# Revit family: MV8-252(280_335_400_450)WV2GN1(PRO)
name_source: partatom
category: Mechanical Equipment
revit_build: Autodesk Revit 2013 (Build: 20120221_2030(x64)
units: mm (PartAtom-declared; Revit-internal decimal feet)

## types (5) — shared parameters
Casing color = White
Compressor = 1
Condensation = Air
Depth = 825 mm  [stored 2.70669 ft]
Description = High efficiency air cooled
Gas = R410A
Height = 1760 mm  [stored 5.77428 ft]
Installation = Outdoor installation
Machine material = Galvanized Steel
Power supply = 380-415V, 3N , 50Hz
Series = VRF
Width = 940 mm  [stored 3.08399 ft]
clearance access behind = 1000 mm  [stored 3.28084 ft]
clearance access front = 1000 mm  [stored 3.28084 ft]
clearance access left = 1000 mm  [stored 3.28084 ft]
clearance access right = 1000 mm  [stored 3.28084 ft]

## per-type parameters (varying)
| type | Air Flow | Cooling Capacity | Cooling Power Input | Gas pipe | Gas pipe Radius | Heating Capacity | Heating Power Input | Liquid pipe | Liquid pipe Radius | Maximum Fuse Amps | Minimum Circuit Amps | Net Weight |
| 12HP | 13500.000 m³/h | 33.500 kW | 13.500 kW | 25.4 mm  [stored 0.0833333 ft] | 12.7 mm  [stored 0.0416667 ft] | 33.500 kW | 10.800 kW | 12.7 mm  [stored 0.0416667 ft] | 6.35 mm  [stored 0.0208333 ft] | 32 A | 23 A | 195.00 kg |
| 10HP | 12600.000 m³/h | 28.000 kW | 9.900 kW | 25.4 mm  [stored 0.0833333 ft] | 12.7 mm  [stored 0.0416667 ft] | 28.000 kW | 7.500 kW | 12.7 mm  [stored 0.0416667 ft] | 6.35 mm  [stored 0.0208333 ft] | 25 A | 19 A | 195.00 kg |
| 8HP | 12600.000 m³/h | 25.200 kW | 8.400 kW | 25.4 mm  [stored 0.0833333 ft] | 12.7 mm  [stored 0.0416667 ft] | 25.200 kW | 6.600 kW | 12.7 mm  [stored 0.0416667 ft] | 6.35 mm  [stored 0.0208333 ft] | 20 A | 17 A | 195.00 kg |
| 14HP | 15600.000 m³/h | 40.000 kW | 17.000 kW | 28.6 mm | 14.3 mm | 40.000 kW | 11.600 kW | 15.9 mm  [stored 0.0521654 ft] | 7.95 mm  [stored 0.0260827 ft] | 32 A | 26 A | 215.00 kg |
| 16HP | 15600.000 m³/h | 45.000 kW | 22.000 kW | 28.6 mm | 14.3 mm | 45.000 kW | 14.000 kW | 15.9 mm  [stored 0.0521654 ft] | 7.95 mm  [stored 0.0260827 ft] | 40 A | 31 A | 215.00 kg |

note: column(s) folded — value = type name in every type: Model

note: [stored X ft] marks values corroborated as IEEE doubles in the binary element streams (Revit-internal decimal feet)

## geometry (parser evidence)
native form markers: Blend x1, Sweep x19
no freeform markers — native parametric forms only
